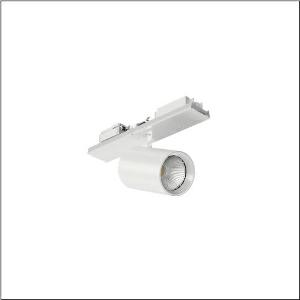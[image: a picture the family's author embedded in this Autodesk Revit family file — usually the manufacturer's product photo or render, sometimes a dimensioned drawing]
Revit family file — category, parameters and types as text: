
# Revit family: licross_r__spot_31_51sl137a45b_29a8
name_source: partatom
category: Lighting Fixtures
units: mm (PartAtom-declared; Revit-internal decimal feet)

## family parameters
Cut with Voids When Loaded = No
Host = Face
Light Source = No
Part Type = Normal
Room Calculation Point = No
Round Connector Dimension = Use Diameter
Shared = No

## types (1)
- --- (1 x LED, 5190 lm, 42.6 W, 4000K)
    Apparent Load = 43 VA
    CIE Flux Codes = 92 97 99 100 100
    Color Rendering = 90
    Color Temperature = 4000K
    Default Elevation = 1800 mm
    Description = Licross® Spot 31, directional spotlight, light control with lens, of plastic, LED rated luminous flux: 5.190lm, light colour: 940, with plug, 3-pole, with phase selection, mains connection: 220..240V, AC, 50/60Hz, of aluminium, traffic white (RAL 9016), length: 140mm, diameter: 90mm, protection rating (complete): IP20, insulation class (complete): insulation class I (protective earthing), certification: CE, packaging unit: 1 piece
    Height = 175 mm
    Lamp = 1 x LED
    Lamp Light Flux = 5190 lm
    Lamp Power = 42.6 W
    Lamp count = 1
    Length = 90 mm
    Luminous efficacy = 122 lm/W
    Manufacturer = Siteco
    ModVariant = No
    Model = 51SL137A45B
    Mounting Place = Ceiling
    Mounting Type = Pendant
    Number of Poles = 1
    OnlyDefault = Yes
    Power Factor = 1
    Product Name = Licross® Spot 31
    Product group = directional spotlight
    ProductGroupID = 905
    Protection Class = Protection class I
    Protection Degree = IP 20
    RLX_Detail_Level = 1
    RLX_Emergency_Light_Flux = 0 lm
    RLX_Emergency_Type = 0
    RLX_Emergency_Type_DB = No
    RlxData = <blob elided: 14809 chars, md5=2532b571>
    Socket = socket
    Standby Power = 0 W
    System Light Flux = 5190 lm
    System Power = 43 W
    Type Comments = factory setting: luminous flux: 100 % | (ON | ON | ON) | 1050 mA
    Type Image = l_1245720.jpg
    URL = http://relux.com
    VarID = @adj_081923
    Voltage = 0 V
    Weight = 0.00 kg
    Width = 0 mm  [stored 0 ft]

note: [stored X ft] marks values corroborated as IEEE doubles in the binary element streams (Revit-internal decimal feet)

## geometry (parser evidence)
native form markers: Sweep x12
no freeform markers — native parametric forms only
